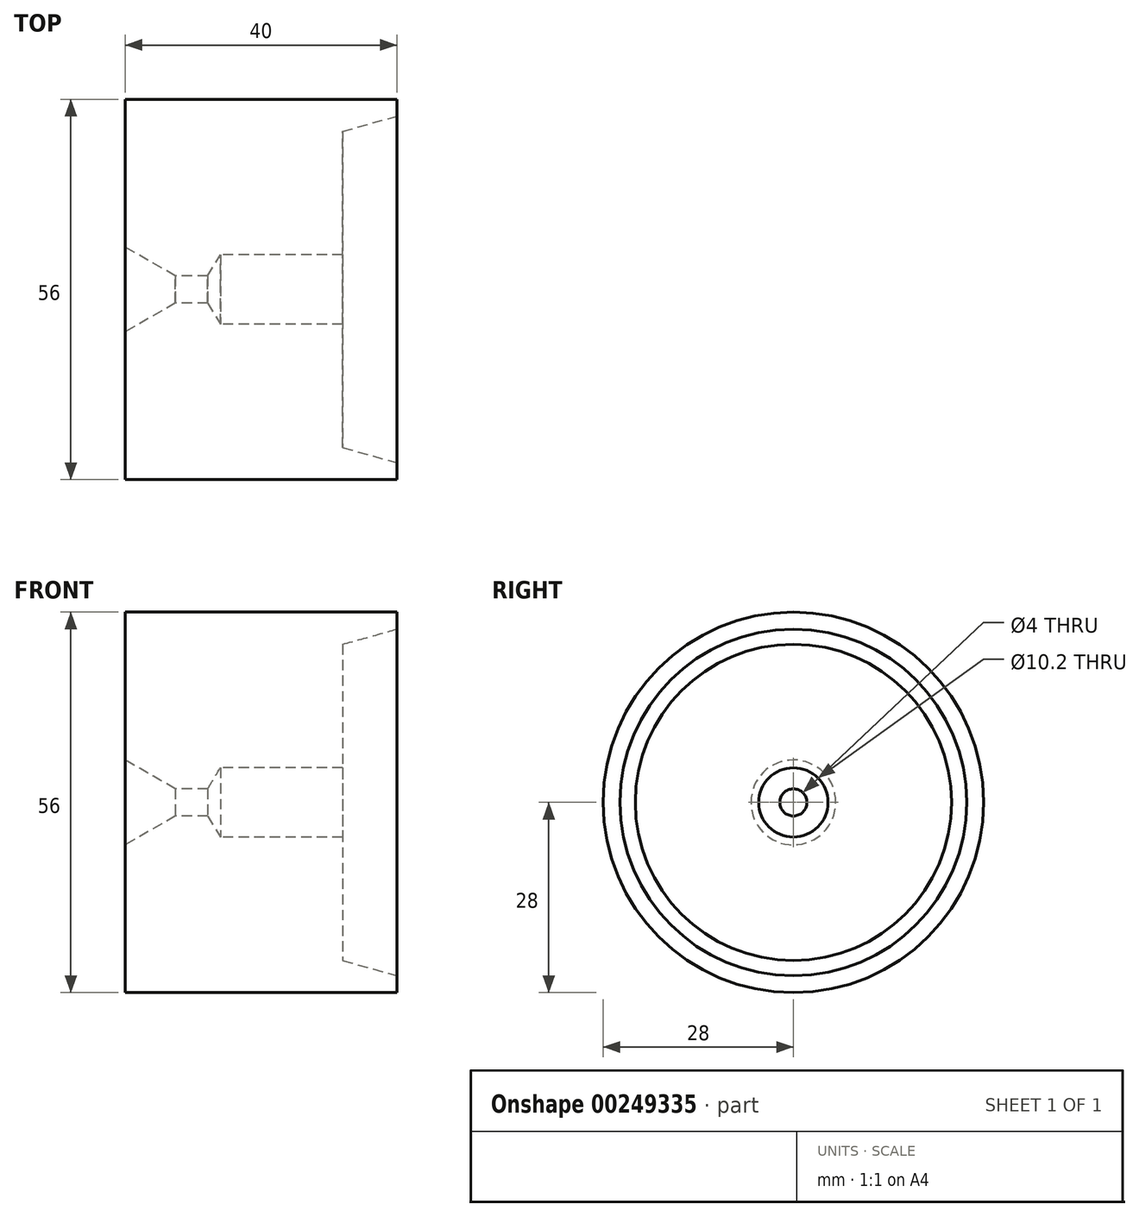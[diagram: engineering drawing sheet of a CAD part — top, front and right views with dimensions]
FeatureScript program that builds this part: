
annotation { "Feature Type Name" : "Feature", "Feature Type Description" : "" }
export const myFeature = defineFeature(function(context is Context, id is Id, definition is map)
    precondition{}
    {
        {
            var Q0;
            Q0=qCreatedBy(makeId("Front.planeOp"),FACE);
            var sketch = newSketch(context, id + "F0", { "sketchPlane" : qUnion([Q0])});
            skLineSegment(sketch, "E0", {"start": v(-12.55, 0) * mm, "end": v(0, 0) * mm, "construction": true});
            skLineSegment(sketch, "E1", {"start": v(0, 5.1) * mm, "end": v(0, 23.83) * mm, "construction": true});
            skLineSegment(sketch, "E2", {"start": v(0, 23.83) * mm, "end": v(6, 25.5) * mm, "construction": true});
            skLineSegment(sketch, "E3", {"start": v(6, 25.5) * mm, "end": v(6, 28) * mm});
            skLineSegment(sketch, "E4", {"start": v(6, 28) * mm, "end": v(-34, 28) * mm});
            skLineSegment(sketch, "E5", {"start": v(-2, 5.1) * mm, "end": v(-20, 5.1) * mm});
            skLineSegment(sketch, "E6", {"start": v(0, 23.83) * mm, "end": v(12.27, 23.83) * mm, "construction": true});
            skLineSegment(sketch, "E7", {"start": v(6, 25.5) * mm, "end": v(-2, 23.27) * mm});
            skLineSegment(sketch, "E8", {"start": v(-2, 23.27) * mm, "end": v(-2, 5.1) * mm});
            skLineSegment(sketch, "E9", {"start": v(-34, 28) * mm, "end": v(-34, 6.25) * mm});
            skLineSegment(sketch, "E10", {"start": v(-21.86, 2) * mm, "end": v(-20, 5.1) * mm});
            skLineSegment(sketch, "E11", {"start": v(-21.86, 2) * mm, "end": v(-26.64, 2) * mm});
            skLineSegment(sketch, "E12", {"start": v(-26.64, 2) * mm, "end": v(-34, 6.25) * mm});
            skLineSegment(sketch, "E13", {"start": v(-26.64, 2) * mm, "end": v(-23.17, 0) * mm, "construction": true});
            skSolve(sketch);
        }
        {
            var Q0;
            Q0=makeQuery(id+"F0.imprint","IMPRINT",FACE,{"disambiguationData":[TD([[makeQuery(id+"F0.imprint","IMPRINT",EDGE,{"derivedFrom":sQuery(id+"F0.wireOp",EDGE,"E3")}),1.0]])]});
            var Q1;
            Q1=sQuery(id+"F0.wireOp",EDGE,"E0");
            revolve(context, id + "F1", {"entities" : qUnion([Q0]), "axis" : qUnion([Q1]), "revolveType" : RevolveType.FULL});
        }
    });
